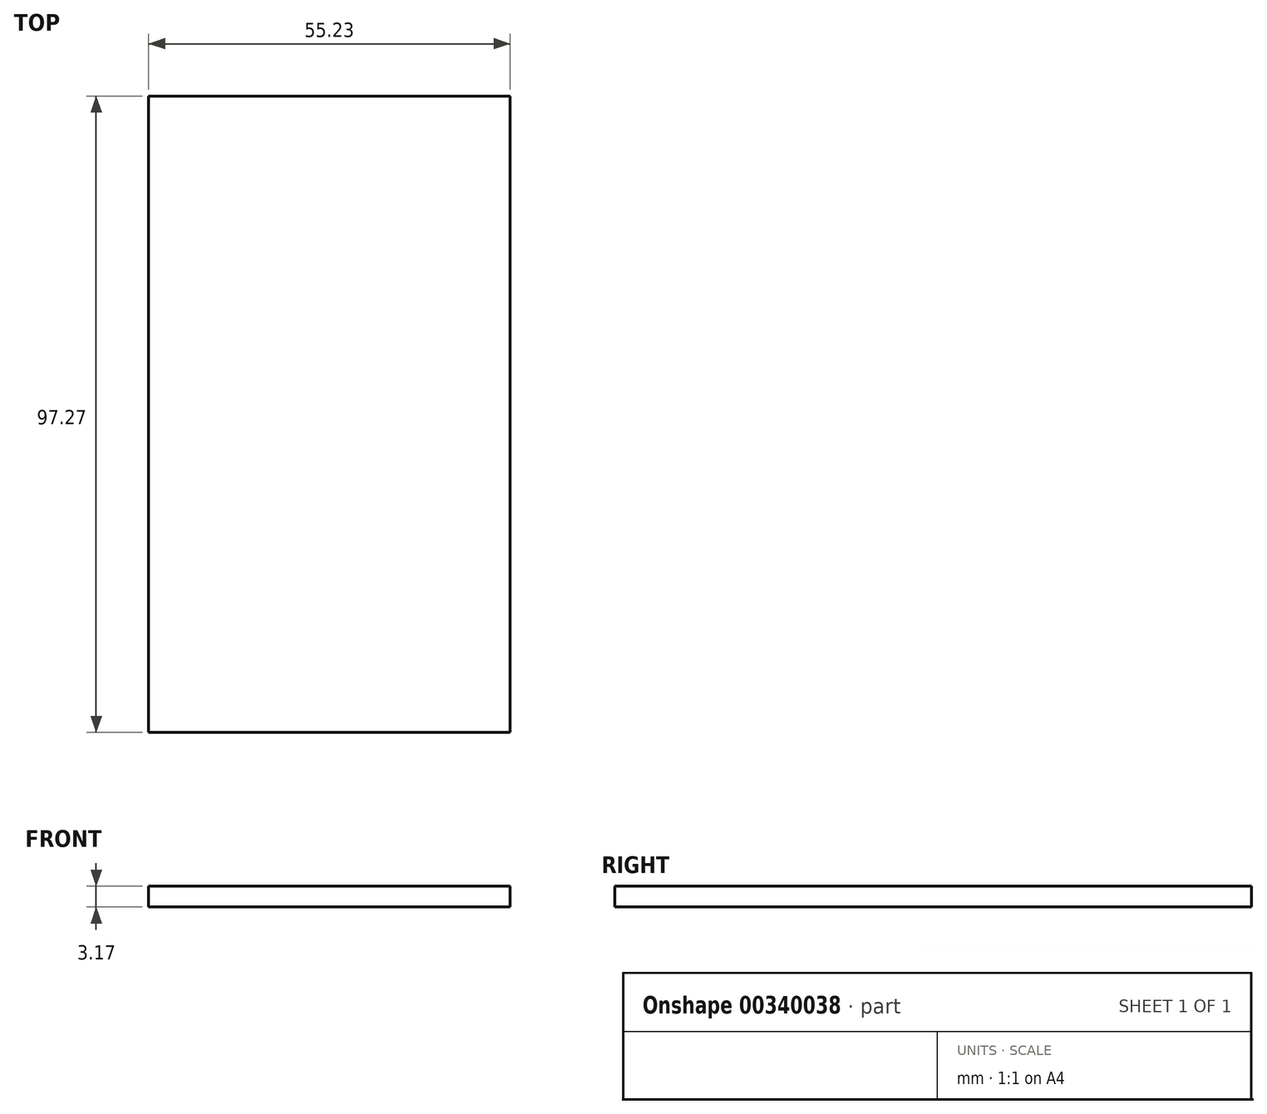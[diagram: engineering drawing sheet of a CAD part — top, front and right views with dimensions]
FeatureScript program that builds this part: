
annotation { "Feature Type Name" : "Feature", "Feature Type Description" : "" }
export const myFeature = defineFeature(function(context is Context, id is Id, definition is map)
    precondition{}
    {
        {
            var Q0;
            Q0=qCreatedBy(makeId("Top.planeOp"),FACE);
            var sketch = newSketch(context, id + "F0", { "sketchPlane" : qUnion([Q0])});
            skLineSegment(sketch, "E0.bottom", {"start": v(-33.19, 31.46) * mm, "end": v(22.04, 31.46) * mm});
            skLineSegment(sketch, "E0.top", {"start": v(-33.19, -65.8) * mm, "end": v(22.04, -65.8) * mm});
            skLineSegment(sketch, "E0.left", {"start": v(-33.19, 31.46) * mm, "end": v(-33.19, -65.8) * mm});
            skLineSegment(sketch, "E0.right", {"start": v(22.04, 31.46) * mm, "end": v(22.04, -65.8) * mm});
            skSolve(sketch);
        }
        {
            var Q0;
            Q0=makeQuery(id+"F0.imprint","IMPRINT",FACE,{"disambiguationData":[TD([[makeQuery(id+"F0.imprint","IMPRINT",EDGE,{"derivedFrom":sQuery(id+"F0.wireOp",EDGE,"E0.bottom")}),-1.0]])]});
            extrude(context, id + "F1", {"entities" : qUnion([Q0]), "depth" : 3.17 * mm});
        }
    });
